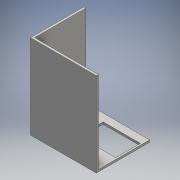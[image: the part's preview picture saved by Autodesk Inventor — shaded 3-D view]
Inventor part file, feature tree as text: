
AUTODESK INVENTOR PART (.ipt)
format: ipt  version: 2016 (Build 200138000, 138)  size: 116,736 bytes
history: native  units: mm
features: extrude x3, sketch x3
ambient origin geometry x8: Origin, YZ Plane, XZ Plane, XY Plane, X Axis, Y Axis, Z Axis, Center Point
bodies: 实体1 (feature_tree)
feature tree (6):
  extrude  "拉伸1"  Depth=252.5mm
  extrude  "拉伸2"  Depth=7.5mm
  extrude  "拉伸3"  Depth=117.0mm
  sketch  "草图1"  dims[d0=312.5mm d1=252.5mm]
  sketch  "草图3"  dims[d2=36.0mm d3=7.5mm]
  sketch  "草图4"  dims[d4=177.0mm d5=117.0mm d6=10.0mm d7=0.0mm d10=390.0mm d11=0.0mm d13=10.0mm d14=390.0mm d15=0.0mm d16=10.0mm]
